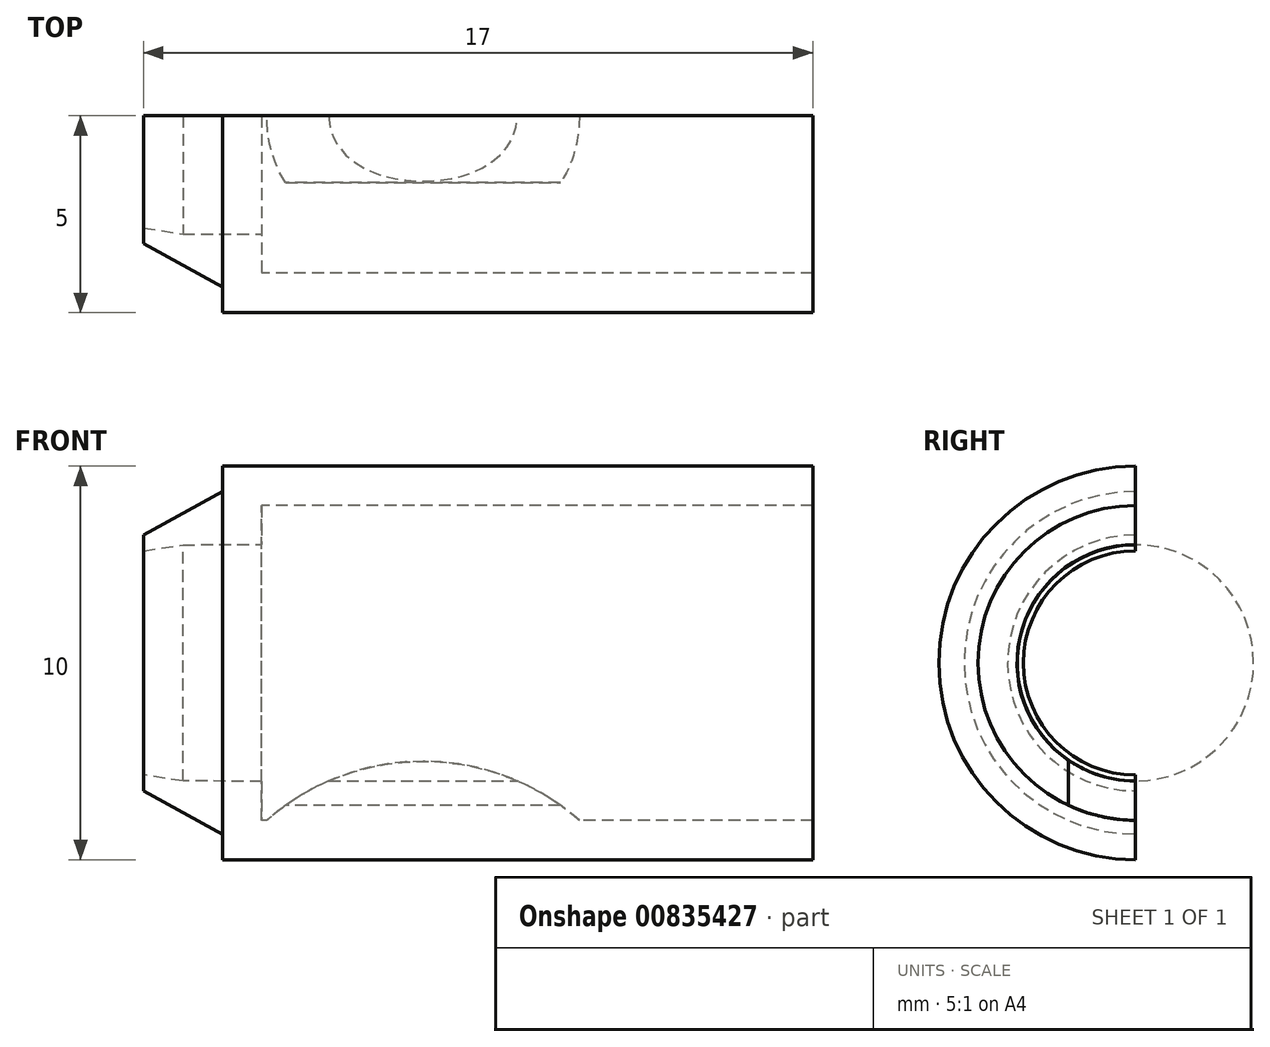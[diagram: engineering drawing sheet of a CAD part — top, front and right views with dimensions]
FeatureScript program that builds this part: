
annotation { "Feature Type Name" : "Feature", "Feature Type Description" : "" }
export const myFeature = defineFeature(function(context is Context, id is Id, definition is map)
    precondition{}
    {
        {
            var Q0;
            Q0=qCreatedBy(makeId("Front.planeOp"),FACE);
            var sketch = newSketch(context, id + "F0", { "sketchPlane" : qUnion([Q0])});
            skLineSegment(sketch, "E0", {"start": v(0, 0) * mm, "end": v(0, 2.85) * mm});
            skLineSegment(sketch, "E1", {"start": v(0, 2.85) * mm, "end": v(0, 3.25) * mm});
            skLineSegment(sketch, "E2", {"start": v(0, 3.25) * mm, "end": v(2, 4.35) * mm});
            skLineSegment(sketch, "E3", {"start": v(2, 4.35) * mm, "end": v(2, 5) * mm});
            skLineSegment(sketch, "E4", {"start": v(2, 5) * mm, "end": v(17, 5) * mm});
            skLineSegment(sketch, "E5", {"start": v(1, 3) * mm, "end": v(0, 2.85) * mm});
            skLineSegment(sketch, "E6", {"start": v(1, 3) * mm, "end": v(3, 3) * mm});
            skLineSegment(sketch, "E7", {"start": v(17, 4) * mm, "end": v(17, 5) * mm});
            skLineSegment(sketch, "E8", {"start": v(3, 3) * mm, "end": v(3, 4) * mm});
            skLineSegment(sketch, "E9", {"start": v(3, 4) * mm, "end": v(17, 4) * mm});
            skLineSegment(sketch, "E10", {"start": v(0, 0) * mm, "end": v(16.17, 0) * mm});
            skSolve(sketch);
        }
        {
            var Q0;
            Q0 = qSketchRegion(id + "F0", true);
            var Q1;
            Q1=sQuery(id+"F0.wireOp",EDGE,"E10");
            revolve(context, id + "F1", {"surfaceOperationType" : NewSurfaceOperationType.NEW, "entities" : qUnion([Q0]), "axis" : qUnion([Q1]), "revolveType" : RevolveType.FULL});
        }
        {
            var Q0;
            Q0=makeQuery(id+"F1.opRevolve","SWEPT_FACE",FACE,{"disambiguationData":[OSD([sQuery(id+"F0.wireOp",EDGE,"E7")])]});
            var sketch = newSketch(context, id + "F2", { "sketchPlane" : qUnion([Q0])});
            skLineSegment(sketch, "E11", {"start": v(0, 0) * mm, "end": v(0, 8.3) * mm});
            skLineSegment(sketch, "E12", {"start": v(0, -8.21) * mm, "end": v(0, 0) * mm});
            skLineSegment(sketch, "E13", {"start": v(0, 8.3) * mm, "end": v(10.23, 8.3) * mm});
            skLineSegment(sketch, "E14", {"start": v(10.23, 8.3) * mm, "end": v(10.23, -8.38) * mm});
            skLineSegment(sketch, "E15", {"start": v(10.23, -8.38) * mm, "end": v(0, -8.21) * mm});
            skSolve(sketch);
        }
        {
            var Q0;
            Q0 = qSketchRegion(id + "F2", true);
            extrude(context, id + "F3", {"entities" : qUnion([Q0]), "operationType" : NewBodyOperationType.REMOVE, "oppositeDirection" : true, "depth" : 25 * mm, "offsetDistance" : 25 * mm});
        }
        {
            var Q0;
            Q0=makeQuery(id+"F3.boolean.opBoolean","COPY",FACE,{"disambiguationData":[OD(1.0)],"derivedFrom":makeQuery(id+"F3.opExtrude","SWEPT_FACE",FACE,{"disambiguationData":[OSD([sQuery(id+"F2.wireOp",EDGE,"E11"),sQuery(id+"F2.wireOp",EDGE,"E12")])]})});
            var sketch = newSketch(context, id + "F4", { "sketchPlane" : qUnion([Q0])});
            skCircle(sketch, "E16", {"center": v(-7.1, 8.5) * mm, "radius": 6 * mm});
            skLineSegment(sketch, "E17", {"start": v(-3, 3.01) * mm, "end": v(-3, -2.8) * mm});
            skLineSegment(sketch, "E18", {"start": v(0, 2.85) * mm, "end": v(0, 1.05) * mm});
            skLineSegment(sketch, "E19", {"start": v(-11.07, 4) * mm, "end": v(-3, 4) * mm});
            skPoint(sketch, "E19.startSnap0", {"position": v(-10, 4) * mm});
            skCircle(sketch, "E20.1.0", {"center": v(-7.1, -8.5) * mm, "radius": 6 * mm});
            skLineSegment(sketch, "E20.1.1", {"start": v(-3.13, -4) * mm, "end": v(-11.2, -4) * mm});
            skPoint(sketch, "E20.center", {"position": v(-7.1, 0) * mm});
            skSolve(sketch);
        }
        {
            var Q0;
            {var subQ0=sQuery(id+"F4.wireOp",EDGE,"E20.1.1");var subQ1=sQuery(id+"F4.wireOp",EDGE,"E20.1.0");var subQ2=makeQuery(id+"F4.imprint","INTERSECT",VERTEX,{"disambiguationData":[OD(0.0)],"derivedFrom":[subQ1,subQ0]});Q0=makeQuery(id+"F4.imprint","IMPRINT",FACE,{"disambiguationData":[TD([[makeQuery(id+"F4.imprint","IMPRINT",EDGE,{"disambiguationData":[TD([[subQ2,-1.0]])],"derivedFrom":subQ1}),1.0]])]});}
            extrude(context, id + "F5", {"entities" : qUnion([Q0]), "operationType" : NewBodyOperationType.ADD, "oppositeDirection" : true, "depth" : 1.7 * mm, "offsetDistance" : 25 * mm});
        }
        {
            var Q0;
            Q0=makeQuery(id+"F1.opRevolve","SWEPT_FACE",FACE,{"disambiguationData":[OSD([sQuery(id+"F0.wireOp",EDGE,"E7")])]});
            var sketch = newSketch(context, id + "F6", { "sketchPlane" : qUnion([Q0])});
            skCircle(sketch, "E21", {"center": v(0, 0) * mm, "radius": 3 * mm});
            skSolve(sketch);
        }
        {
            var Q0;
            Q0 = qSketchRegion(id + "F6", true);
            extrude(context, id + "F7", {"entities" : qUnion([Q0]), "operationType" : NewBodyOperationType.REMOVE, "oppositeDirection" : true, "depth" : 12.88 * mm, "offsetDistance" : 25 * mm});
        }
    });
